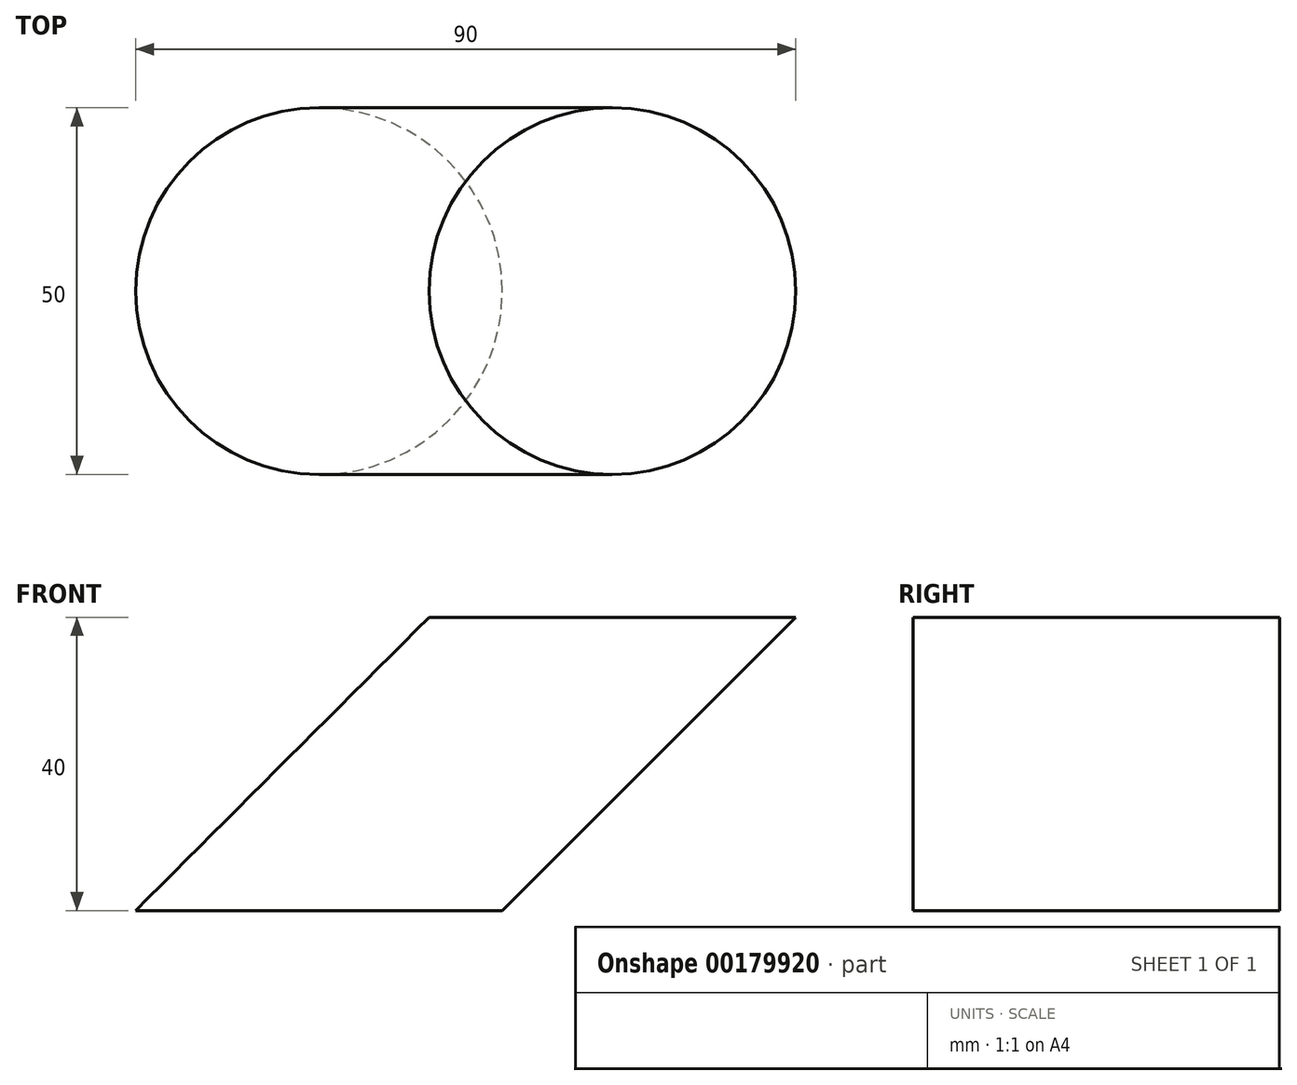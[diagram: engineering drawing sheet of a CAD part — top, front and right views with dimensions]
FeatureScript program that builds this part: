
annotation { "Feature Type Name" : "Feature", "Feature Type Description" : "" }
export const myFeature = defineFeature(function(context is Context, id is Id, definition is map)
    precondition{}
    {
        {
            var Q0;
            Q0=qCreatedBy(makeId("Top.planeOp"),FACE);
            var sketch = newSketch(context, id + "F0", { "sketchPlane" : qUnion([Q0])});
            skCircle(sketch, "E0", {"center": v(0, 0) * mm, "radius": 25 * mm});
            skSolve(sketch);
        }
        {
            var Q0;
            Q0=qCreatedBy(makeId("Front.planeOp"),FACE);
            var sketch = newSketch(context, id + "F1", { "sketchPlane" : qUnion([Q0])});
            skLineSegment(sketch, "E1", {"start": v(0, 0) * mm, "end": v(40, 40) * mm, "construction": true});
            skLineSegment(sketch, "E2", {"start": v(40, 40) * mm, "end": v(40, 0) * mm, "construction": true});
            skLineSegment(sketch, "E3", {"start": v(40, 0) * mm, "end": v(0, 0) * mm, "construction": true});
            skLineSegment(sketch, "E4", {"start": v(0, 0) * mm, "end": v(40, 40) * mm});
            skSolve(sketch);
        }
        {
            var Q0;
            Q0=makeQuery(id+"F0.imprint","IMPRINT",FACE,{"disambiguationData":[TD([[makeQuery(id+"F0.imprint","IMPRINT",EDGE,{"derivedFrom":sQuery(id+"F0.wireOp",EDGE,"E0")}),1.0]])]});
            var Q1;
            Q1 = qConstructionFilter(qBodyType(qCreatedBy(id + "F1" ,EDGE), BodyType.WIRE), ConstructionObject.NO);
            sweep(context, id + "F2", {"profiles" : qUnion([Q0]), "path" : qUnion([Q1])});
        }
    });
